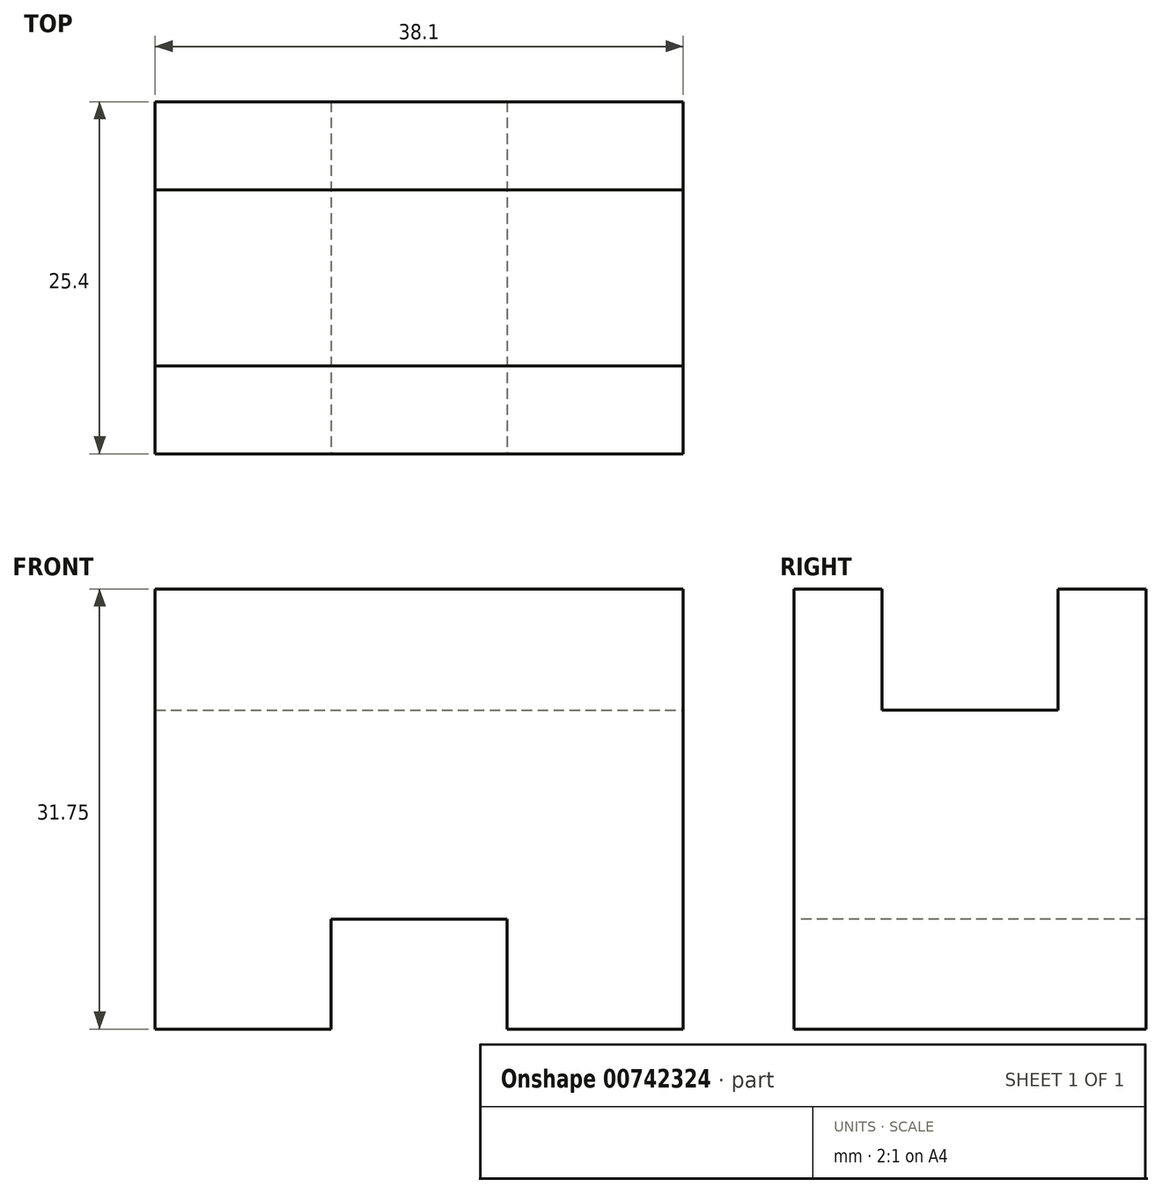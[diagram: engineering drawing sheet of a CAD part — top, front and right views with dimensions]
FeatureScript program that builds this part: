
annotation { "Feature Type Name" : "Feature", "Feature Type Description" : "" }
export const myFeature = defineFeature(function(context is Context, id is Id, definition is map)
    precondition{}
    {
        {
            var Q0;
            Q0=qCreatedBy(makeId("Right.planeOp"),FACE);
            var sketch = newSketch(context, id + "F0", { "sketchPlane" : qUnion([Q0])});
            skLineSegment(sketch, "E0", {"start": v(0, 0) * mm, "end": v(-25.4, 0) * mm});
            skLineSegment(sketch, "E1", {"start": v(-25.4, 0) * mm, "end": v(-25.4, 31.75) * mm});
            skLineSegment(sketch, "E2", {"start": v(-25.4, 31.75) * mm, "end": v(0, 31.75) * mm});
            skLineSegment(sketch, "E3", {"start": v(0, 31.75) * mm, "end": v(0, 0) * mm});
            skSolve(sketch);
        }
        {
            var Q0;
            Q0 = qSketchRegion(id + "F0", true);
            extrude(context, id + "F1", {"entities" : qUnion([Q0]), "depth" : 38.1 * mm, "offsetDistance" : 25.4 * mm});
        }
        {
            var Q0;
            Q0=makeQuery(id+"F1.opExtrude","CAP_FACE",FACE,{"disambiguationData":[OSD([sQuery(id+"F0.wireOp",EDGE,"E0"),sQuery(id+"F0.wireOp",EDGE,"E1"),sQuery(id+"F0.wireOp",EDGE,"E2"),sQuery(id+"F0.wireOp",EDGE,"E3")])],"isStart":false});
            var sketch = newSketch(context, id + "F2", { "sketchPlane" : qUnion([Q0])});
            skLineSegment(sketch, "E4", {"start": v(-19.05, 31.75) * mm, "end": v(-19.05, 23.02) * mm});
            skLineSegment(sketch, "E5", {"start": v(-19.05, 23.02) * mm, "end": v(-6.35, 23.02) * mm});
            skLineSegment(sketch, "E6", {"start": v(-6.35, 23.02) * mm, "end": v(-6.35, 31.75) * mm});
            skSolve(sketch);
        }
        {
            var Q0;
            Q0 = qSketchRegion(id + "F2", true);
            var Q1;
            {var subQ0=sQuery(id+"F2.wireOp",EDGE,"E4");Q1=makeQuery(id+"F2.imprint","IMPRINT",FACE,{"disambiguationData":[TD([[makeQuery(id+"F2.imprint","IMPRINT",EDGE,{"derivedFrom":subQ0}),1.0]])]});}
            extrude(context, id + "F3", {"entities" : qUnion([Q0, Q1]), "operationType" : NewBodyOperationType.REMOVE, "endBound" : BoundingType.THROUGH_ALL, "oppositeDirection" : true, "depth" : 25.4 * mm, "offsetDistance" : 25.4 * mm});
        }
        {
            var Q0;
            Q0=makeQuery(id+"F1.opExtrude","SWEPT_FACE",FACE,{"disambiguationData":[OSD([sQuery(id+"F0.wireOp",EDGE,"E1")])]});
            var sketch = newSketch(context, id + "F4", { "sketchPlane" : qUnion([Q0])});
            skLineSegment(sketch, "E7", {"start": v(12.7, 0) * mm, "end": v(12.7, 7.94) * mm});
            skLineSegment(sketch, "E8", {"start": v(12.7, 7.94) * mm, "end": v(25.4, 7.94) * mm});
            skLineSegment(sketch, "E9", {"start": v(25.4, 7.94) * mm, "end": v(25.4, 0) * mm});
            skSolve(sketch);
        }
        {
            var Q0;
            Q0 = qSketchRegion(id + "F4", true);
            var Q1;
            {var subQ0=sQuery(id+"F4.wireOp",EDGE,"E7");Q1=makeQuery(id+"F4.imprint","IMPRINT",FACE,{"disambiguationData":[TD([[makeQuery(id+"F4.imprint","IMPRINT",EDGE,{"derivedFrom":subQ0}),-1.0]])]});}
            extrude(context, id + "F5", {"entities" : qUnion([Q0, Q1]), "operationType" : NewBodyOperationType.REMOVE, "endBound" : BoundingType.THROUGH_ALL, "oppositeDirection" : true, "depth" : 25.4 * mm, "offsetDistance" : 25.4 * mm});
        }
    });
